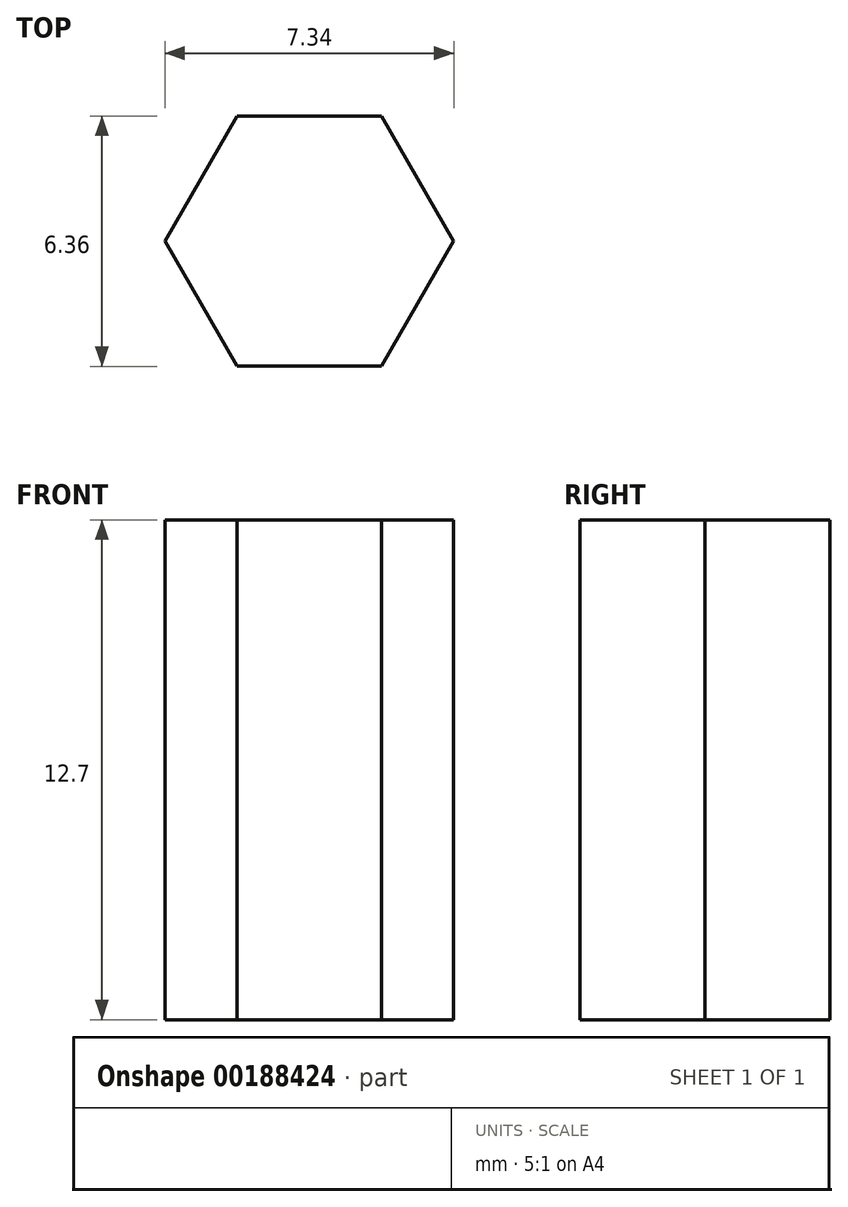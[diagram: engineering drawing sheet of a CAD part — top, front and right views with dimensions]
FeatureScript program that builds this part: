
annotation { "Feature Type Name" : "Feature", "Feature Type Description" : "" }
export const myFeature = defineFeature(function(context is Context, id is Id, definition is map)
    precondition{}
    {
        {
            var Q0;
            Q0=qCreatedBy(makeId("Top.planeOp"),FACE);
            var sketch = newSketch(context, id + "F0", { "sketchPlane" : qUnion([Q0])});
            skCircle(sketch, "E0.cCircle", {"center": v(0, 0) * mm, "radius": 3.17 * mm, "construction": true});
            skLineSegment(sketch, "E0.0", {"start": v(-1.83, 3.18) * mm, "end": v(1.83, 3.17) * mm});
            skLineSegment(sketch, "E0.1", {"start": v(1.83, 3.17) * mm, "end": v(3.67, 0) * mm});
            skLineSegment(sketch, "E0.2", {"start": v(3.67, 0) * mm, "end": v(1.83, -3.18) * mm});
            skLineSegment(sketch, "E0.3", {"start": v(1.83, -3.18) * mm, "end": v(-1.83, -3.18) * mm});
            skLineSegment(sketch, "E0.4", {"start": v(-1.83, -3.18) * mm, "end": v(-3.67, 0) * mm});
            skLineSegment(sketch, "E0.5", {"start": v(-3.67, 0) * mm, "end": v(-1.83, 3.18) * mm});
            skPoint(sketch, "E0.0.midPoint", {"position": v(0, 3.18) * mm});
            skSolve(sketch);
        }
        {
            var Q0;
            Q0=makeQuery(id+"F0.imprint","IMPRINT",FACE,{"disambiguationData":[TD([[makeQuery(id+"F0.imprint","IMPRINT",EDGE,{"derivedFrom":sQuery(id+"F0.wireOp",EDGE,"E0.0")}),-1.0]])]});
            extrude(context, id + "F1", {"entities" : qUnion([Q0]), "depth" : 12.7 * mm});
        }
    });
